annotation { "Feature Type Name" : "Feature", "Feature Type Description" : "" }
export const myFeature = defineFeature(function(context is Context, id is Id, definition is map)
    precondition{}
    {
        {
            var Q0;
            Q0=qCreatedBy(makeId("Front.planeOp"),FACE);
            var sketch = newSketch(context, id + "F0", { "sketchPlane" : qUnion([Q0])});
            skLineSegment(sketch, "E0.bottom", {"start": v(-54.96, 30.24) * mm, "end": v(8.54, 30.24) * mm});
            skLineSegment(sketch, "E0.top", {"start": v(-54.96, 11.19) * mm, "end": v(8.54, 11.19) * mm});
            skLineSegment(sketch, "E0.left", {"start": v(-58.14, 27.06) * mm, "end": v(-58.14, 14.36) * mm});
            skLineSegment(sketch, "E0.right", {"start": v(11.71, 27.06) * mm, "end": v(11.71, 14.36) * mm});
            skPoint(sketch, "E1.visualSharp", {"position": v(-58.14, 30.24) * mm});
            skArc(sketch, "E1.filletArc", {"start": v(-54.96, 30.24) * mm, "mid": v(-57.2, 29.3) * mm, "end": v(-58.14, 27.06) * mm});
            skPoint(sketch, "E2.visualSharp", {"position": v(11.71, 30.24) * mm});
            skArc(sketch, "E2.filletArc", {"start": v(11.71, 27.06) * mm, "mid": v(10.78, 29.3) * mm, "end": v(8.54, 30.24) * mm});
            skPoint(sketch, "E3.visualSharp", {"position": v(11.71, 11.19) * mm});
            skArc(sketch, "E3.filletArc", {"start": v(8.54, 11.19) * mm, "mid": v(10.78, 12.12) * mm, "end": v(11.71, 14.36) * mm});
            skPoint(sketch, "E4.visualSharp", {"position": v(-58.14, 11.19) * mm});
            skArc(sketch, "E4.filletArc", {"start": v(-58.14, 14.36) * mm, "mid": v(-57.2, 12.12) * mm, "end": v(-54.96, 11.19) * mm});
            skCircle(sketch, "E5", {"center": v(6.94, 20.93) * mm, "radius": 2.03 * mm});
            skSolve(sketch);
        }
        {
            var Q0;
            Q0=makeQuery(id+"F0.imprint","IMPRINT",FACE,{"disambiguationData":[TD([[makeQuery(id+"F0.imprint","IMPRINT",EDGE,{"derivedFrom":sQuery(id+"F0.wireOp",EDGE,"E0.bottom")}),-1.0]])]});
            extrude(context, id + "F1", {"entities" : qUnion([Q0]), "depth" : 2.54 * mm, "offsetDistance" : 25.4 * mm});
        }
        {
            var Q0;
            Q0=makeQuery(id+"F1.opExtrude","CAP_FACE",FACE,{"disambiguationData":[OSD([sQuery(id+"F0.wireOp",EDGE,"E0.bottom"),sQuery(id+"F0.wireOp",EDGE,"E0.top"),sQuery(id+"F0.wireOp",EDGE,"E0.left"),sQuery(id+"F0.wireOp",EDGE,"E0.right"),sQuery(id+"F0.wireOp",EDGE,"E1.filletArc"),sQuery(id+"F0.wireOp",EDGE,"E2.filletArc"),sQuery(id+"F0.wireOp",EDGE,"E3.filletArc"),sQuery(id+"F0.wireOp",EDGE,"E4.filletArc"),sQuery(id+"F0.wireOp",EDGE,"E5")])],"isStart":false});
            var sketch = newSketch(context, id + "F2", { "sketchPlane" : qUnion([Q0])});
            skText(sketch, "E6", { "text": "PANTHER PROUD", "fontName": "RobotoSlab-Regular.ttf"});
            const initialGuessF2  = {"E6": [-0.0523, 0.01836, 1, 0, 0.00427]};
            skSetInitialGuess(sketch, initialGuessF2);
            skSolve(sketch);
        }
        {
            var Q0;
            Q0 = qSketchRegion(id + "F2", true);
            extrude(context, id + "F3", {"entities" : qUnion([Q0]), "operationType" : NewBodyOperationType.ADD, "depth" : 0.76 * mm, "offsetDistance" : 25.4 * mm});
        }
    });